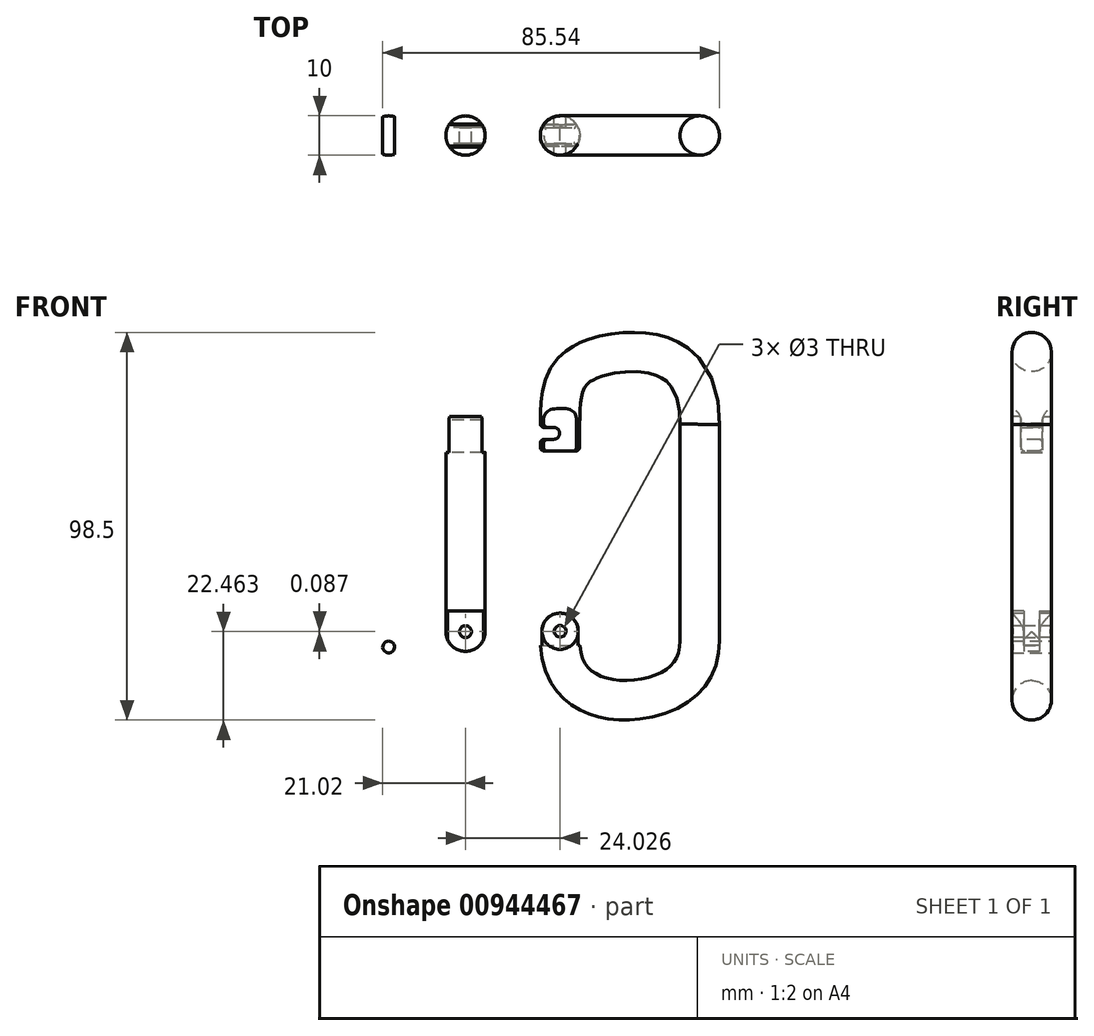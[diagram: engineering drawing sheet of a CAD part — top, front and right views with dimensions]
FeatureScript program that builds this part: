
annotation { "Feature Type Name" : "Feature", "Feature Type Description" : "" }
export const myFeature = defineFeature(function(context is Context, id is Id, definition is map)
    precondition{}
    {
        {
            var Q0;
            Q0=qCreatedBy(makeId("Front.planeOp"),FACE);
            var sketch = newSketch(context, id + "F0", { "sketchPlane" : qUnion([Q0])});
            skLineSegment(sketch, "E0", {"start": v(29.03, 26.87) * mm, "end": v(29.03, -28.13) * mm});
            skFitSpline(sketch, "E1", {"points": [v(29.03, 26.87) * mm, v(24.05, 41.4) * mm, v(12.25, 45.24) * mm, v(-2.3, 41.3) * mm, v(-6.48, 26.87) * mm], "startDerivative": vector(1.57, 78.74) * mm, "endDerivative": vector(-0.78, -90) * mm});
            skLineSegment(sketch, "E2", {"start": v(29.03, -14.7) * mm, "end": v(34.03, -14.7) * mm});
            skLineSegment(sketch, "E3", {"start": v(34.03, -14.7) * mm, "end": v(34.03, -11.2) * mm});
            skLineSegment(sketch, "E4", {"start": v(34.03, -11.2) * mm, "end": v(29.03, -11.2) * mm});
            skLineSegment(sketch, "E5", {"start": v(-6.48, 26.87) * mm, "end": v(-6.48, 20.1) * mm});
            skFitSpline(sketch, "E6", {"points": [v(29.03, -28.13) * mm, v(19.35, -41.56) * mm, v(1.88, -41.72) * mm, v(-6.48, -28.13) * mm], "startDerivative": vector(-0.5, -68.85) * mm, "endDerivative": vector(0, 65.2) * mm});
            skLineSegment(sketch, "E7", {"start": v(-6.48, -28.13) * mm, "end": v(-6.48, -21.11) * mm});
            skSolve(sketch);
        }
        {
            var Q0;
            Q0=sQuery(id+"F0.wireOp",EDGE,"E2");
            var Q1;
            Q1=sQuery(id+"F0.wireOp",EDGE,"E0");
            revolve(context, id + "F1", {"bodyType" : ToolBodyType.SURFACE, "surfaceOperationType" : NewSurfaceOperationType.NEW, "surfaceEntities" : qUnion([Q0]), "axis" : qUnion([Q1]), "revolveType" : RevolveType.FULL});
        }
        {
            var Q0;
            Q0=makeQuery(id+"F1.opRevolve","SWEPT_FACE",FACE,{"disambiguationData":[OSD([sQuery(id+"F0.wireOp",EDGE,"E2")])]});
            var Q1;
            Q1=sQuery(id+"F0.wireOp",EDGE,"E0");
            var Q2;
            Q2=sQuery(id+"F0.wireOp",EDGE,"E1");
            var Q3;
            Q3=sQuery(id+"F0.wireOp",EDGE,"E5");
            var Q4;
            Q4=sQuery(id+"F0.wireOp",EDGE,"E6");
            var Q5;
            Q5=sQuery(id+"F0.wireOp",EDGE,"E7");
            sweep(context, id + "F2", {"profiles" : qUnion([Q0]), "path" : qUnion([Q1, Q2, Q3, Q4, Q5])});
        }
        {
            var Q0;
            Q0=qCreatedBy(makeId("Right.planeOp"),FACE);
            cPlane(context, id + "F3", {"entities" : qUnion([Q0]), "cplaneType" : CPlaneType.OFFSET, "offset" : 12 * mm, "oppositeDirection" : true, "width" : 150 * mm, "height" : 150 * mm});
        }
        {
            var Q0;
            Q0=qCreatedBy(id+"F3.planeOp",FACE);
            var sketch = newSketch(context, id + "F4", { "sketchPlane" : qUnion([Q0])});
            skLineSegment(sketch, "E8", {"start": v(0, 0) * mm, "end": v(0, 18.8) * mm});
            skLineSegment(sketch, "E9", {"start": v(-2.75, 19.5) * mm, "end": v(-2.75, 27.77) * mm});
            skLineSegment(sketch, "E10", {"start": v(-5.98, 27.77) * mm, "end": v(-5.98, 19.5) * mm});
            skLineSegment(sketch, "E11", {"start": v(-5.98, 19.5) * mm, "end": v(-2.75, 19.5) * mm});
            skLineSegment(sketch, "E12.MirrorCS", {"start": v(2.75, 19.5) * mm, "end": v(2.75, 27.77) * mm});
            skLineSegment(sketch, "E13.MirrorCS", {"start": v(5.98, 27.77) * mm, "end": v(5.98, 19.5) * mm});
            skLineSegment(sketch, "E14.MirrorCS", {"start": v(5.98, 27.77) * mm, "end": v(6.03, 27.77) * mm});
            skLineSegment(sketch, "E15.MirrorCS", {"start": v(5.98, 19.5) * mm, "end": v(2.75, 19.5) * mm});
            skArc(sketch, "E16", {"start": v(5.98, 31.06) * mm, "mid": v(3.7, 30.08) * mm, "end": v(2.75, 27.77) * mm});
            skLineSegment(sketch, "E17", {"start": v(5.98, 27.77) * mm, "end": v(5.98, 31.77) * mm});
            skPoint(sketch, "E18.orphan", {"position": v(2.75, 27.77) * mm});
            skArc(sketch, "E19.MirrorCS", {"start": v(-5.98, 31.06) * mm, "mid": v(-3.7, 30.08) * mm, "end": v(-2.75, 27.77) * mm});
            skLineSegment(sketch, "E20.MirrorCS", {"start": v(-5.98, 27.77) * mm, "end": v(-5.98, 31.77) * mm});
            skSolve(sketch);
        }
        {
            var Q0;
            Q0=makeQuery(id+"F4.imprint","IMPRINT",FACE,{"disambiguationData":[TD([[makeQuery(id+"F4.imprint","IMPRINT",EDGE,{"derivedFrom":sQuery(id+"F4.wireOp",EDGE,"E12.MirrorCS")}),-1.0]])]});
            var Q1;
            Q1=makeQuery(id+"F4.imprint","IMPRINT",FACE,{"disambiguationData":[TD([[makeQuery(id+"F4.imprint","IMPRINT",EDGE,{"derivedFrom":sQuery(id+"F4.wireOp",EDGE,"E9")}),1.0]])]});
            extrude(context, id + "F5", {"entities" : qUnion([Q0, Q1]), "operationType" : NewBodyOperationType.REMOVE, "depth" : 25 * mm, "offsetDistance" : 25 * mm});
        }
        {
            var Q0;
            Q0=makeQuery(id+"F5.boolean.opBoolean","COPY",FACE,{"derivedFrom":makeQuery(id+"F5.opExtrude","SWEPT_FACE",FACE,{"disambiguationData":[OSD([sQuery(id+"F4.wireOp",EDGE,"E9")])]})});
            var sketch = newSketch(context, id + "F6", { "sketchPlane" : qUnion([Q0])});
            skLineSegment(sketch, "E21", {"start": v(-8.05, 24.56) * mm, "end": v(-14.39, 24.56) * mm});
            skArc(sketch, "E22.0.startCap", {"start": v(-8.05, 26.06) * mm, "mid": v(-6.55, 24.56) * mm, "end": v(-8.05, 23.06) * mm});
            skArc(sketch, "E22.0.endCap", {"start": v(-14.39, 23.06) * mm, "mid": v(-15.89, 24.56) * mm, "end": v(-14.39, 26.06) * mm});
            skLineSegment(sketch, "E22.0.left", {"start": v(-8.05, 23.06) * mm, "end": v(-14.39, 23.06) * mm});
            skLineSegment(sketch, "E22.0.right", {"start": v(-8.05, 26.06) * mm, "end": v(-14.39, 26.06) * mm});
            skSolve(sketch);
        }
        {
            var Q0;
            Q0 = qSketchRegion(id + "F6", true);
            extrude(context, id + "F7", {"entities" : qUnion([Q0]), "operationType" : NewBodyOperationType.REMOVE, "oppositeDirection" : true, "depth" : 25 * mm, "offsetDistance" : 25 * mm});
        }
        {
            var Q0;
            Q0=makeQuery(id+"F7.boolean.opBoolean","COPY",EDGE,{"derivedFrom":makeQuery(id+"F7.opExtrude","CAP_EDGE",EDGE,{"disambiguationData":[OSD([sQuery(id+"F6.wireOp",EDGE,"E22.0.right")])],"isStart":true})});
            var Q1;
            Q1=makeQuery(id+"F7.boolean.opBoolean","INTERSECT",EDGE,{"derivedFrom":[makeQuery(id+"F5.boolean.opBoolean","SPLIT",FACE,{"disambiguationData":[OD(0.0)],"derivedFrom":makeQuery(id+"F2.opSweep","SWEPT_FACE",FACE,{"disambiguationData":[OSD([sQuery(id+"F0.wireOp",VERTEX,"E2.end"),sQuery(id+"F0.wireOp",EDGE,"E5")])]})}),makeQuery(id+"F7.opExtrude","SWEPT_FACE",FACE,{"disambiguationData":[OSD([sQuery(id+"F6.wireOp",EDGE,"E22.0.right")])]})]});
            var Q2;
            Q2=makeQuery(id+"F7.boolean.opBoolean","INTERSECT",EDGE,{"derivedFrom":[makeQuery(id+"F5.boolean.opBoolean","SPLIT",FACE,{"disambiguationData":[OD(0.0)],"derivedFrom":makeQuery(id+"F2.opSweep","SWEPT_FACE",FACE,{"disambiguationData":[OSD([sQuery(id+"F0.wireOp",VERTEX,"E2.end"),sQuery(id+"F0.wireOp",EDGE,"E5")])]})}),makeQuery(id+"F7.opExtrude","SWEPT_FACE",FACE,{"disambiguationData":[OSD([sQuery(id+"F6.wireOp",EDGE,"E22.0.left")])]})]});
            var Q3;
            Q3=makeQuery(id+"F7.boolean.opBoolean","INTERSECT",EDGE,{"derivedFrom":[makeQuery(id+"F5.boolean.opBoolean","COPY",FACE,{"derivedFrom":makeQuery(id+"F5.opExtrude","SWEPT_FACE",FACE,{"disambiguationData":[OSD([sQuery(id+"F4.wireOp",EDGE,"E12.MirrorCS")])]})}),makeQuery(id+"F7.opExtrude","SWEPT_FACE",FACE,{"disambiguationData":[OSD([sQuery(id+"F6.wireOp",EDGE,"E22.0.left")])]})]});
            var Q4;
            Q4=makeQuery(id+"F2.opSweep","CAP_FACE",FACE,{"disambiguationData":[OSD([sQuery(id+"F0.wireOp",VERTEX,"E5.end"),sQuery(id+"F0.wireOp",EDGE,"E2")])],"isStart":true});
            fillet(context, id + "F8", {"entities" : qUnion([Q0, Q1, Q2, Q3, Q4]), "radius" : 1 * mm, "tangentPropagation" : true, "allowEdgeOverflow" : false});
        }
        {
            var Q0;
            Q0=qCreatedBy(makeId("Front.planeOp"),FACE);
            cPlane(context, id + "F9", {"entities" : qUnion([Q0]), "cplaneType" : CPlaneType.OFFSET, "offset" : (5.5 / 2) * mm, "width" : 150 * mm, "height" : 150 * mm});
        }
        {
            var Q0;
            Q0=qCreatedBy(makeId("Right.planeOp"),FACE);
            var sketch = newSketch(context, id + "F10", { "sketchPlane" : qUnion([Q0])});
            skLineSegment(sketch, "E23", {"start": v(0, -29.34) * mm, "end": v(-2, -29.34) * mm});
            skLineSegment(sketch, "E24", {"start": v(-2, -29.34) * mm, "end": v(-2, -20.74) * mm});
            skLineSegment(sketch, "E25", {"start": v(-2, -20.74) * mm, "end": v(0, -20.74) * mm});
            skLineSegment(sketch, "E26.MirrorCS", {"start": v(2, -29.34) * mm, "end": v(2, -20.74) * mm});
            skLineSegment(sketch, "E27.MirrorCS", {"start": v(2, -20.74) * mm, "end": v(0, -20.74) * mm});
            skLineSegment(sketch, "E28.MirrorCS", {"start": v(0, -29.34) * mm, "end": v(2, -29.34) * mm});
            skSolve(sketch);
        }
        {
            var Q0;
            Q0 = qSketchRegion(id + "F10", true);
            extrude(context, id + "F11", {"entities" : qUnion([Q0]), "operationType" : NewBodyOperationType.REMOVE, "oppositeDirection" : true, "depth" : 25 * mm, "offsetDistance" : 25 * mm});
        }
        {
            var Q0;
            Q0=qCreatedBy(id+"F9.planeOp",FACE);
            var sketch = newSketch(context, id + "F12", { "sketchPlane" : qUnion([Q0])});
            skCircle(sketch, "E29", {"center": v(-6.45, -25.71) * mm, "radius": 1.5 * mm});
            skCircle(sketch, "E30", {"center": v(-6.45, -25.71) * mm, "radius": 4.6 * mm});
            skLineSegment(sketch, "E31", {"start": v(-6.45, -25.71) * mm, "end": v(-0.5, -25.71) * mm});
            skLineSegment(sketch, "E32", {"start": v(-0.5, -25.71) * mm, "end": v(-12.4, -25.71) * mm});
            skLineSegment(sketch, "E33", {"start": v(-1.85, -25.71) * mm, "end": v(-1.85, -20.58) * mm});
            skLineSegment(sketch, "E34", {"start": v(-1.85, -20.58) * mm, "end": v(-11.22, -20.58) * mm});
            skLineSegment(sketch, "E35", {"start": v(-11.22, -20.58) * mm, "end": v(-11.22, -25.71) * mm});
            skSolve(sketch);
        }
        {
            var Q0;
            {var subQ0=sQuery(id+"F12.wireOp",EDGE,"E33");Q0=makeQuery(id+"F12.imprint","IMPRINT",FACE,{"disambiguationData":[TD([[makeQuery(id+"F12.imprint","IMPRINT",EDGE,{"derivedFrom":subQ0}),1.0]])]});}
            var Q1;
            {var subQ0=sQuery(id+"F12.wireOp",EDGE,"E31");var subQ1=sQuery(id+"F12.wireOp",EDGE,"E29");var subQ2=makeQuery(id+"F12.imprint","INTERSECT",VERTEX,{"derivedFrom":[subQ1,subQ0]});Q1=makeQuery(id+"F12.imprint","IMPRINT",FACE,{"disambiguationData":[TD([[makeQuery(id+"F12.imprint","IMPRINT",EDGE,{"disambiguationData":[TD([[subQ2,-1.0]])],"derivedFrom":subQ1}),1.0]])]});}
            var Q2;
            {var subQ0=sQuery(id+"F12.wireOp",EDGE,"E31");var subQ1=sQuery(id+"F12.wireOp",EDGE,"E29");var subQ2=makeQuery(id+"F12.imprint","INTERSECT",VERTEX,{"derivedFrom":[subQ1,subQ0]});Q2=makeQuery(id+"F12.imprint","IMPRINT",FACE,{"disambiguationData":[TD([[makeQuery(id+"F12.imprint","IMPRINT",EDGE,{"disambiguationData":[TD([[subQ2,1.0]])],"derivedFrom":subQ1}),1.0]])]});}
            extrude(context, id + "F13", {"entities" : qUnion([Q0, Q1, Q2]), "operationType" : NewBodyOperationType.REMOVE, "endBound" : BoundingType.SYMMETRIC, "depth" : 25 * mm, "offsetDistance" : 25 * mm});
        }
        {
            var Q0;
            Q0=qCreatedBy(makeId("Front.planeOp"),FACE);
            var sketch = newSketch(context, id + "F14", { "sketchPlane" : qUnion([Q0])});
            skLineSegment(sketch, "E36", {"start": v(-6.45, -25.71) * mm, "end": v(-31.45, -25.71) * mm});
            skLineSegment(sketch, "E37", {"start": v(-6.45, -25.71) * mm, "end": v(-6.45, 24.54) * mm});
            skLineSegment(sketch, "E38", {"start": v(-6.45, 24.54) * mm, "end": v(-31.45, 24.54) * mm});
            skCircle(sketch, "E39", {"center": v(-50, -29.74) * mm, "radius": 1.5 * mm});
            skLineSegment(sketch, "E40", {"start": v(-31.45, -25.71) * mm, "end": v(-31.45, 27.18) * mm});
            skLineSegment(sketch, "E41", {"start": v(-31.45, 27.18) * mm, "end": v(-7.35, 27.18) * mm});
            skCircle(sketch, "E42", {"center": v(-31.45, -25.71) * mm, "radius": 5 * mm});
            skCircle(sketch, "E43", {"center": v(-31.45, -25.71) * mm, "radius": 1.5 * mm});
            skLineSegment(sketch, "E44", {"start": v(-26.45, -25.71) * mm, "end": v(-26.45, 27.18) * mm});
            skSolve(sketch);
        }
        {
            var Q0;
            Q0=makeQuery(id+"F14.imprint","IMPRINT",FACE,{"disambiguationData":[TD([[makeQuery(id+"F14.imprint","IMPRINT",EDGE,{"derivedFrom":sQuery(id+"F14.wireOp",EDGE,"E39")}),1.0]])]});
            extrude(context, id + "F15", {"entities" : qUnion([Q0]), "endBound" : BoundingType.SYMMETRIC, "depth" : 10 * mm, "offsetDistance" : 25 * mm});
        }
        {
            var Q0;
            Q0=qCreatedBy(makeId("Top.planeOp"),FACE);
            var sketch = newSketch(context, id + "F16", { "sketchPlane" : qUnion([Q0])});
            skCircle(sketch, "E45", {"center": v(-50, 0) * mm, "radius": 5 * mm});
            skCircle(sketch, "E46", {"center": v(-50, 0) * mm, "radius": 6.4 * mm});
            skSolve(sketch);
        }
        {
            var Q0;
            Q0=makeQuery(id+"F16.imprint","IMPRINT",FACE,{"disambiguationData":[TD([[makeQuery(id+"F16.imprint","IMPRINT",EDGE,{"derivedFrom":sQuery(id+"F16.wireOp",EDGE,"E45")}),-1.0]])]});
            extrude(context, id + "F17", {"entities" : qUnion([Q0]), "operationType" : NewBodyOperationType.REMOVE, "oppositeDirection" : true, "depth" : 40.8 * mm, "offsetDistance" : 25 * mm});
        }
        {
            var Q0;
            Q0=qCreatedBy(makeId("Front.planeOp"),FACE);
            var sketch = newSketch(context, id + "F18", { "sketchPlane" : qUnion([Q0])});
            skLineSegment(sketch, "E47", {"start": v(-6.46, -25.8) * mm, "end": v(-30.48, -25.8) * mm});
            skLineSegment(sketch, "E48", {"start": v(-30.48, -25.8) * mm, "end": v(-30.48, 24.65) * mm});
            skLineSegment(sketch, "E49", {"start": v(-30.48, 24.65) * mm, "end": v(10.79, 24.65) * mm});
            skLineSegment(sketch, "E50", {"start": v(-30.48, -25.8) * mm, "end": v(-35.48, -25.8) * mm});
            skLineSegment(sketch, "E51", {"start": v(-35.48, -25.8) * mm, "end": v(-35.48, 24.65) * mm});
            skLineSegment(sketch, "E52", {"start": v(-6.3, 28.86) * mm, "end": v(-30.48, 28.86) * mm});
            skLineSegment(sketch, "E53", {"start": v(-30.48, 24.65) * mm, "end": v(-30.48, 28.86) * mm});
            skLineSegment(sketch, "E54", {"start": v(-35.48, 24.65) * mm, "end": v(-35.48, 28.86) * mm});
            skLineSegment(sketch, "E55", {"start": v(-30.48, 28.86) * mm, "end": v(-35.48, 28.86) * mm});
            skPoint(sketch, "E56.orphan", {"position": v(-35.48, 28.86) * mm});
            skCircle(sketch, "E57", {"center": v(-30.48, -25.8) * mm, "radius": 5 * mm});
            skLineSegment(sketch, "E58", {"start": v(-30.48, -25.8) * mm, "end": v(-30.48, -30.8) * mm});
            skLineSegment(sketch, "E59", {"start": v(-30.48, -30.8) * mm, "end": v(-35.48, -30.8) * mm});
            skLineSegment(sketch, "E60", {"start": v(-35.48, -25.8) * mm, "end": v(-35.48, -30.8) * mm});
            skLineSegment(sketch, "E61.MirrorCS", {"start": v(-30.48, -30.8) * mm, "end": v(-25.48, -30.8) * mm});
            skLineSegment(sketch, "E62.MirrorCS", {"start": v(-25.48, -25.8) * mm, "end": v(-25.48, -30.8) * mm});
            skCircle(sketch, "E63", {"center": v(-30.48, -25.8) * mm, "radius": 1.5 * mm});
            skSolve(sketch);
        }
        {
            var Q0;
            {var subQ1=sQuery(id+"F18.wireOp",EDGE,"E51");Q0=makeQuery(id+"F18.imprint","IMPRINT",FACE,{"disambiguationData":[TD([[makeQuery(id+"F18.imprint","IMPRINT",EDGE,{"derivedFrom":subQ1}),-1.0]])]});}
            var Q1;
            {var subQ0=sQuery(id+"F18.wireOp",EDGE,"E50");Q1=makeQuery(id+"F18.imprint","IMPRINT",FACE,{"disambiguationData":[TD([[makeQuery(id+"F18.imprint","IMPRINT",EDGE,{"derivedFrom":subQ0}),-1.0]])]});}
            var Q2;
            {var subQ0=sQuery(id+"F18.wireOp",EDGE,"E50");Q2=makeQuery(id+"F18.imprint","IMPRINT",FACE,{"disambiguationData":[TD([[makeQuery(id+"F18.imprint","IMPRINT",EDGE,{"derivedFrom":subQ0}),1.0]])]});}
            var Q3;
            {var subQ2=sQuery(id+"F18.wireOp",EDGE,"E59");Q3=makeQuery(id+"F18.imprint","IMPRINT",FACE,{"disambiguationData":[TD([[makeQuery(id+"F18.imprint","IMPRINT",EDGE,{"derivedFrom":subQ2}),-1.0]])]});}
            var Q4;
            {var subQ0=sQuery(id+"F18.wireOp",EDGE,"E57");var subQ1=sQuery(id+"F18.wireOp",EDGE,"E48");var subQ2=makeQuery(id+"F18.imprint","INTERSECT",VERTEX,{"derivedFrom":[subQ1,subQ0]});Q4=makeQuery(id+"F18.imprint","IMPRINT",FACE,{"disambiguationData":[TD([[makeQuery(id+"F18.imprint","IMPRINT",EDGE,{"disambiguationData":[TD([[subQ2,1.0]])],"derivedFrom":subQ1}),1.0]])]});}
            var Q5;
            {var subQ1=sQuery(id+"F18.wireOp",EDGE,"E50");var subQ3=sQuery(id+"F18.wireOp",EDGE,"E63");var subQ4=makeQuery(id+"F18.imprint","INTERSECT",VERTEX,{"derivedFrom":[subQ1,subQ3]});Q5=makeQuery(id+"F18.imprint","IMPRINT",FACE,{"disambiguationData":[TD([[makeQuery(id+"F18.imprint","IMPRINT",EDGE,{"disambiguationData":[TD([[subQ4,-1.0]])],"derivedFrom":subQ3}),-1.0]])]});}
            var Q6;
            Q6=sQuery(id+"F18.wireOp",EDGE,"E48");
            revolve(context, id + "F19", {"surfaceOperationType" : NewSurfaceOperationType.NEW, "entities" : qUnion([Q0, Q1, Q2, Q3, Q4, Q5]), "axis" : qUnion([Q6]), "revolveType" : RevolveType.FULL});
        }
        {
            var Q0;
            {var subQ2=sQuery(id+"F18.wireOp",EDGE,"E59");Q0=makeQuery(id+"F18.imprint","IMPRINT",FACE,{"disambiguationData":[TD([[makeQuery(id+"F18.imprint","IMPRINT",EDGE,{"derivedFrom":subQ2}),-1.0]])]});}
            var Q1;
            {var subQ0=sQuery(id+"F18.wireOp",EDGE,"E61.MirrorCS");Q1=makeQuery(id+"F18.imprint","IMPRINT",FACE,{"disambiguationData":[TD([[makeQuery(id+"F18.imprint","IMPRINT",EDGE,{"derivedFrom":subQ0}),1.0]])]});}
            extrude(context, id + "F20", {"entities" : qUnion([Q0, Q1]), "operationType" : NewBodyOperationType.REMOVE, "endBound" : BoundingType.SYMMETRIC, "oppositeDirection" : true, "depth" : 25 * mm, "offsetDistance" : 25 * mm});
        }
        {
            var Q0;
            Q0=qCreatedBy(makeId("Right.planeOp"),FACE);
            cPlane(context, id + "F21", {"entities" : qUnion([Q0]), "cplaneType" : CPlaneType.OFFSET, "offset" : 36 * mm, "oppositeDirection" : true, "width" : 150 * mm, "height" : 150 * mm});
        }
        {
            var Q0;
            Q0=qCreatedBy(id+"F21.planeOp",FACE);
            var sketch = newSketch(context, id + "F22", { "sketchPlane" : qUnion([Q0])});
            skLineSegment(sketch, "E64", {"start": v(0, 28.94) * mm, "end": v(0, 19.75) * mm});
            skLineSegment(sketch, "E65", {"start": v(0, 19.75) * mm, "end": v(-2.75, 19.75) * mm});
            skLineSegment(sketch, "E66", {"start": v(-2.75, 19.75) * mm, "end": v(-2.75, 28.84) * mm});
            skLineSegment(sketch, "E67", {"start": v(-2.75, 28.84) * mm, "end": v(0, 28.84) * mm});
            skLineSegment(sketch, "E68.MirrorCS", {"start": v(2.75, 19.75) * mm, "end": v(2.75, 28.84) * mm});
            skLineSegment(sketch, "E69.MirrorCS", {"start": v(2.75, 28.84) * mm, "end": v(0, 28.84) * mm});
            skLineSegment(sketch, "E70.MirrorCS", {"start": v(0, 19.75) * mm, "end": v(2.75, 19.75) * mm});
            skArc(sketch, "E71", {"start": v(5.16, 30.9) * mm, "mid": v(3.47, 29.79) * mm, "end": v(2.75, 27.9) * mm});
            skLineSegment(sketch, "E72", {"start": v(5.16, 30.9) * mm, "end": v(5.16, 19.75) * mm});
            skLineSegment(sketch, "E73", {"start": v(2.75, 19.75) * mm, "end": v(5.16, 19.75) * mm});
            skArc(sketch, "E74.MirrorCS", {"start": v(-5.16, 30.9) * mm, "mid": v(-3.47, 29.79) * mm, "end": v(-2.75, 27.9) * mm});
            skLineSegment(sketch, "E75.MirrorCS", {"start": v(-5.16, 30.9) * mm, "end": v(-5.16, 19.75) * mm});
            skLineSegment(sketch, "E76.MirrorCS", {"start": v(-2.75, 19.75) * mm, "end": v(-5.16, 19.75) * mm});
            skLineSegment(sketch, "E77", {"start": v(3.02, 29.03) * mm, "end": v(-3.02, 29.03) * mm});
            skSolve(sketch);
        }
        {
            var Q0;
            {var subQ5=sQuery(id+"F22.wireOp",EDGE,"E67");Q0=makeQuery(id+"F22.imprint","IMPRINT",FACE,{"disambiguationData":[TD([[makeQuery(id+"F22.imprint","IMPRINT",EDGE,{"derivedFrom":subQ5}),1.0]])]});}
            var Q1;
            {var subQ3=sQuery(id+"F22.wireOp",EDGE,"E65");Q1=makeQuery(id+"F22.imprint","IMPRINT",FACE,{"disambiguationData":[TD([[makeQuery(id+"F22.imprint","IMPRINT",EDGE,{"derivedFrom":subQ3}),-1.0]])]});}
            var Q2;
            {var subQ0=sQuery(id+"F22.wireOp",EDGE,"E69.MirrorCS");Q2=makeQuery(id+"F22.imprint","IMPRINT",FACE,{"disambiguationData":[TD([[makeQuery(id+"F22.imprint","IMPRINT",EDGE,{"derivedFrom":subQ0}),1.0]])]});}
            extrude(context, id + "F23", {"entities" : qUnion([Q0, Q1, Q2]), "operationType" : NewBodyOperationType.REMOVE, "depth" : 12 * mm, "offsetDistance" : 25 * mm});
        }
        {
            var Q0;
            {var subQ1=sQuery(id+"F18.wireOp",EDGE,"E48");var subQ3=sQuery(id+"F18.wireOp",EDGE,"E63");var subQ4=makeQuery(id+"F18.imprint","INTERSECT",VERTEX,{"derivedFrom":[subQ1,subQ3]});Q0=makeQuery(id+"F18.imprint","IMPRINT",FACE,{"disambiguationData":[TD([[makeQuery(id+"F18.imprint","IMPRINT",EDGE,{"disambiguationData":[TD([[subQ4,-1.0]])],"derivedFrom":subQ3}),1.0]])]});}
            var Q1;
            {var subQ1=sQuery(id+"F18.wireOp",EDGE,"E50");var subQ3=sQuery(id+"F18.wireOp",EDGE,"E63");var subQ4=makeQuery(id+"F18.imprint","INTERSECT",VERTEX,{"derivedFrom":[subQ1,subQ3]});Q1=makeQuery(id+"F18.imprint","IMPRINT",FACE,{"disambiguationData":[TD([[makeQuery(id+"F18.imprint","IMPRINT",EDGE,{"disambiguationData":[TD([[subQ4,-1.0]])],"derivedFrom":subQ3}),1.0]])]});}
            var Q2;
            {var subQ1=sQuery(id+"F18.wireOp",EDGE,"E47");var subQ3=sQuery(id+"F18.wireOp",EDGE,"E63");var subQ4=makeQuery(id+"F18.imprint","INTERSECT",VERTEX,{"derivedFrom":[subQ1,subQ3]});Q2=makeQuery(id+"F18.imprint","IMPRINT",FACE,{"disambiguationData":[TD([[makeQuery(id+"F18.imprint","IMPRINT",EDGE,{"disambiguationData":[TD([[subQ4,1.0]])],"derivedFrom":subQ3}),1.0]])]});}
            var Q3;
            {var subQ1=sQuery(id+"F18.wireOp",EDGE,"E47");var subQ3=sQuery(id+"F18.wireOp",EDGE,"E63");var subQ4=makeQuery(id+"F18.imprint","INTERSECT",VERTEX,{"derivedFrom":[subQ1,subQ3]});Q3=makeQuery(id+"F18.imprint","IMPRINT",FACE,{"disambiguationData":[TD([[makeQuery(id+"F18.imprint","IMPRINT",EDGE,{"disambiguationData":[TD([[subQ4,-1.0]])],"derivedFrom":subQ3}),1.0]])]});}
            extrude(context, id + "F24", {"entities" : qUnion([Q0, Q1, Q2, Q3]), "operationType" : NewBodyOperationType.REMOVE, "endBound" : BoundingType.SYMMETRIC, "depth" : 25 * mm, "offsetDistance" : 25 * mm});
        }
        {
            var Q0;
            Q0=qCreatedBy(id+"F21.planeOp",FACE);
            var sketch = newSketch(context, id + "F25", { "sketchPlane" : qUnion([Q0])});
            skLineSegment(sketch, "E78", {"start": v(0, -20.58) * mm, "end": v(-2, -20.58) * mm});
            skLineSegment(sketch, "E79", {"start": v(-2, -20.58) * mm, "end": v(-2, -31.6) * mm});
            skLineSegment(sketch, "E80", {"start": v(-2, -31.6) * mm, "end": v(0, -31.6) * mm});
            skLineSegment(sketch, "E81.MirrorCS", {"start": v(0, -20.58) * mm, "end": v(2, -20.58) * mm});
            skLineSegment(sketch, "E82.MirrorCS", {"start": v(2, -31.6) * mm, "end": v(0, -31.6) * mm});
            skLineSegment(sketch, "E83.MirrorCS", {"start": v(2, -20.58) * mm, "end": v(2, -31.6) * mm});
            skLineSegment(sketch, "E84", {"start": v(-2, -20.58) * mm, "end": v(-5.68, -20.58) * mm});
            skLineSegment(sketch, "E85", {"start": v(-5.68, -20.58) * mm, "end": v(-5.68, -31.6) * mm});
            skLineSegment(sketch, "E86", {"start": v(-5.68, -31.6) * mm, "end": v(-2, -31.6) * mm});
            skLineSegment(sketch, "E87.MirrorCS", {"start": v(2, -20.58) * mm, "end": v(5.68, -20.58) * mm});
            skLineSegment(sketch, "E88.MirrorCS", {"start": v(5.68, -20.58) * mm, "end": v(5.68, -31.6) * mm});
            skLineSegment(sketch, "E89.MirrorCS", {"start": v(5.68, -31.6) * mm, "end": v(2, -31.6) * mm});
            skSolve(sketch);
        }
        {
            var Q0;
            Q0=makeQuery(id+"F25.imprint","IMPRINT",FACE,{"disambiguationData":[TD([[makeQuery(id+"F25.imprint","IMPRINT",EDGE,{"derivedFrom":sQuery(id+"F25.wireOp",EDGE,"E79")}),-1.0]])]});
            var Q1;
            Q1=makeQuery(id+"F25.imprint","IMPRINT",FACE,{"disambiguationData":[TD([[makeQuery(id+"F25.imprint","IMPRINT",EDGE,{"derivedFrom":sQuery(id+"F25.wireOp",EDGE,"E83.MirrorCS")}),1.0]])]});
            extrude(context, id + "F26", {"entities" : qUnion([Q0, Q1]), "operationType" : NewBodyOperationType.REMOVE, "depth" : 14.9 * mm, "offsetDistance" : 25 * mm});
        }
    });
